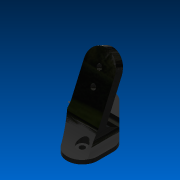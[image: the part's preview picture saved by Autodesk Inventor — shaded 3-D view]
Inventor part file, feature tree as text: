
AUTODESK INVENTOR PART (.ipt)
format: ipt  version: 2022 (Build 260153000, 153)  size: 309,248 bytes
history: native  units: in
note: dims shown in document units (in); Inventor stores cm internally (conversion verified against a paired STEP export)
features: other x6, sketch x5, extrude x5, reference x4, fillet x3, projected_geometry x3, plane x2, hole x2
ambient origin geometry x8: Origin, YZ Plane, XZ Plane, XY Plane, X Axis, Y Axis, Z Axis, Center Point
bodies: Solid1 (feature_tree)
feature tree (30):
  sketch  "Sketch1"  dims[d2=0.9431in d3=1.0in]
  extrude  "Extrusion1"  Depth=1.0in
  plane  "Work Plane1"
  extrude  "Extrusion2"  Depth=0.5in
  hole  "Hole2"  [1 undecoded]
  fillet  "Fillet3"  Radius=1.0in
  fillet  "Fillet2"  Radius=0.125in
  extrude  "Extrusion3"  [1 undecoded]
  hole  "Hole1"  [1 undecoded]
  extrude  "Extrusion4"  Depth=0.25in
  plane  "Work Plane2"
  extrude  "Extrusion5"  Depth=1.0in TaperAngle=0.0deg
  fillet  "Fillet5"  Radius=0.5in
  reference  "Reference1"
  sketch  "Sketch3"  dims[d4=0.5208in d5=0.5in]
  sketch  "Sketch4"  dims[d6=45.0deg d7=1.9074in d8=1.0in d9=0.125in d10=0.0in]
  projected_geometry  "Projected Loop1"
  projected_geometry  "Projected Loop2"
  projected_geometry  "Projected Loop3"
  sketch  "Sketch5"  dims[d11=0.175in d12=0.75in d13=0.35in d14=0.0in d15=0.5635in d16=1.0in d17=0.8108in d18=-0.8191in]
  sketch  "Sketch6"  dims[d20=0.4569in d21=2.1027in d22=0.25in d23=1.0in d24=0.0in d25=0.5in d26=0.8014in d27=0.175in d28=0.75in d29=0.375in d30=0.25in d31=0.5635in d32=1.0in d33=0.8108in d35=0.735in d36=0.0in d37=0.0in d38=0.319in d39=0.5in d41=0.0in d42=0.0in d43=0.45in d44=1.0in d45=0.0in d46=0.225in]
  reference  "Reference2"
  reference  "Reference3"
  reference  "Reference4"
  other  "<userpath>\OneDrive - Auburn University\BasketBall Shooting Robot\Robot.iam"
  other  "Robot.iam"
  other  "Vision Sensor (276-4850):1"
  other  "276-4850-002 Rev30_2"
  other  "276-4850-900 Rev10_3"
  other  "276-4810-907 Rev1_15"
note: 3 required parameter values undecoded (feature->parameter linkage not recoverable at this tier; creation-order binding heuristic only, values carry confidence <= 0.55)
